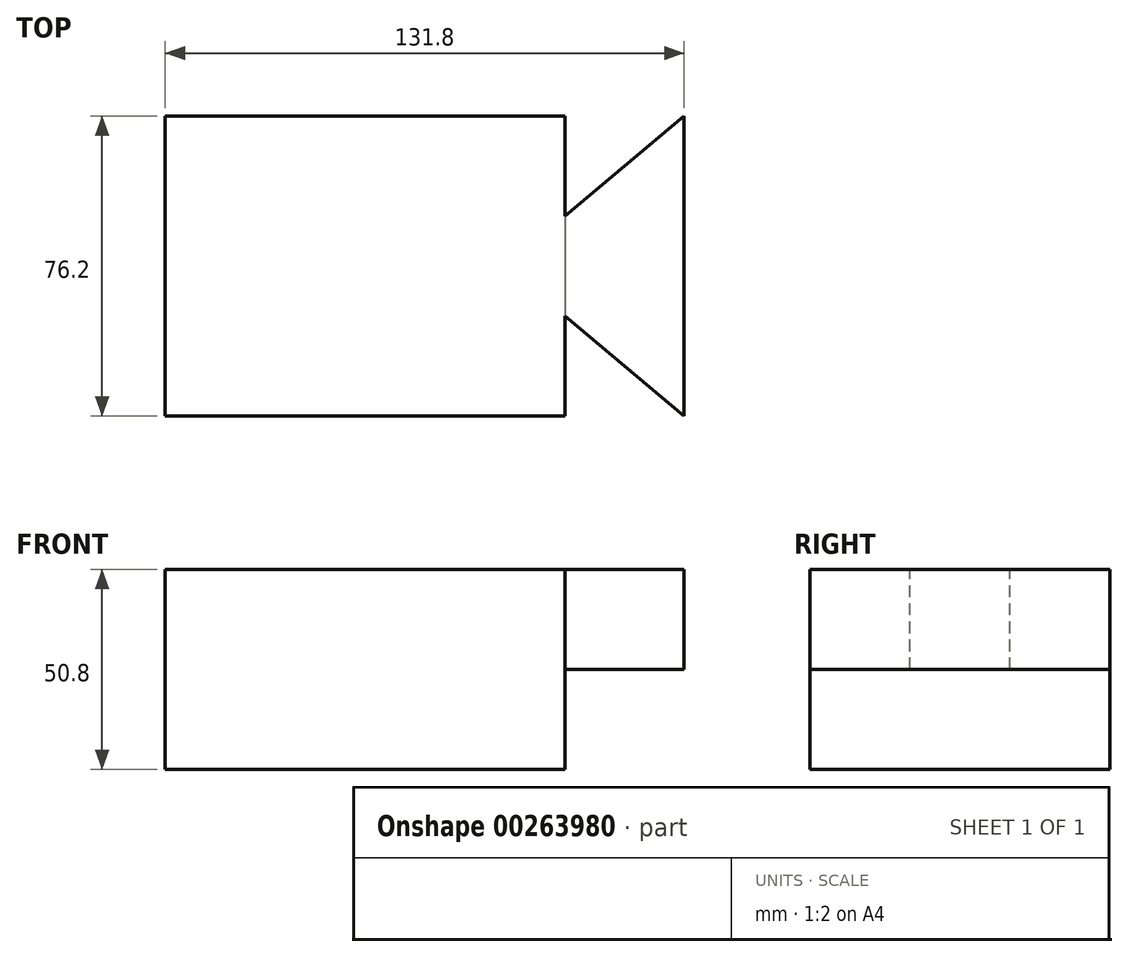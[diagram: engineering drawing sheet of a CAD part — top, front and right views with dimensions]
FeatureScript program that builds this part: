
annotation { "Feature Type Name" : "Feature", "Feature Type Description" : "" }
export const myFeature = defineFeature(function(context is Context, id is Id, definition is map)
    precondition{}
    {
        {
            var Q0;
            Q0=qCreatedBy(makeId("Top.planeOp"),FACE);
            var sketch = newSketch(context, id + "F0", { "sketchPlane" : qUnion([Q0])});
            skLineSegment(sketch, "E0", {"start": v(0, 0) * mm, "end": v(0, 76.2) * mm});
            skLineSegment(sketch, "E1", {"start": v(0, 76.2) * mm, "end": v(101.6, 76.2) * mm});
            skLineSegment(sketch, "E2", {"start": v(101.6, 76.2) * mm, "end": v(101.6, 0) * mm});
            skLineSegment(sketch, "E3", {"start": v(101.6, 0) * mm, "end": v(0, 0) * mm});
            skSolve(sketch);
        }
        {
            var Q0;
            Q0=makeQuery(id+"F0.imprint","IMPRINT",FACE,{"disambiguationData":[TD([[makeQuery(id+"F0.imprint","IMPRINT",EDGE,{"derivedFrom":sQuery(id+"F0.wireOp",EDGE,"E0")}),-1.0]])]});
            extrude(context, id + "F1", {"entities" : qUnion([Q0]), "depth" : 50.8 * mm});
        }
        {
            var Q0;
            Q0=makeQuery(id+"F1.opExtrude","CAP_FACE",FACE,{"disambiguationData":[OSD([sQuery(id+"F0.wireOp",EDGE,"E0"),sQuery(id+"F0.wireOp",EDGE,"E1"),sQuery(id+"F0.wireOp",EDGE,"E2"),sQuery(id+"F0.wireOp",EDGE,"E3")])],"isStart":false});
            var sketch = newSketch(context, id + "F2", { "sketchPlane" : qUnion([Q0])});
            skLineSegment(sketch, "E4", {"start": v(101.6, 0) * mm, "end": v(101.6, 25.4) * mm});
            skLineSegment(sketch, "E5", {"start": v(101.6, 25.4) * mm, "end": v(131.8, 0) * mm});
            skLineSegment(sketch, "E6", {"start": v(131.8, 0) * mm, "end": v(131.8, 76.2) * mm});
            skLineSegment(sketch, "E7", {"start": v(101.6, 76.2) * mm, "end": v(101.6, 50.8) * mm});
            skLineSegment(sketch, "E8", {"start": v(101.6, 50.8) * mm, "end": v(131.8, 76.2) * mm});
            skSolve(sketch);
        }
        {
            var Q0;
            Q0 = qSketchRegion(id + "F2", true);
            var Q1;
            {var subQ0=sQuery(id+"F2.wireOp",EDGE,"E5");Q1=makeQuery(id+"F2.imprint","IMPRINT",FACE,{"disambiguationData":[TD([[makeQuery(id+"F2.imprint","IMPRINT",EDGE,{"derivedFrom":subQ0}),1.0]])]});}
            extrude(context, id + "F3", {"entities" : qUnion([Q0, Q1]), "operationType" : NewBodyOperationType.ADD, "oppositeDirection" : true, "depth" : 25.4 * mm});
        }
    });
